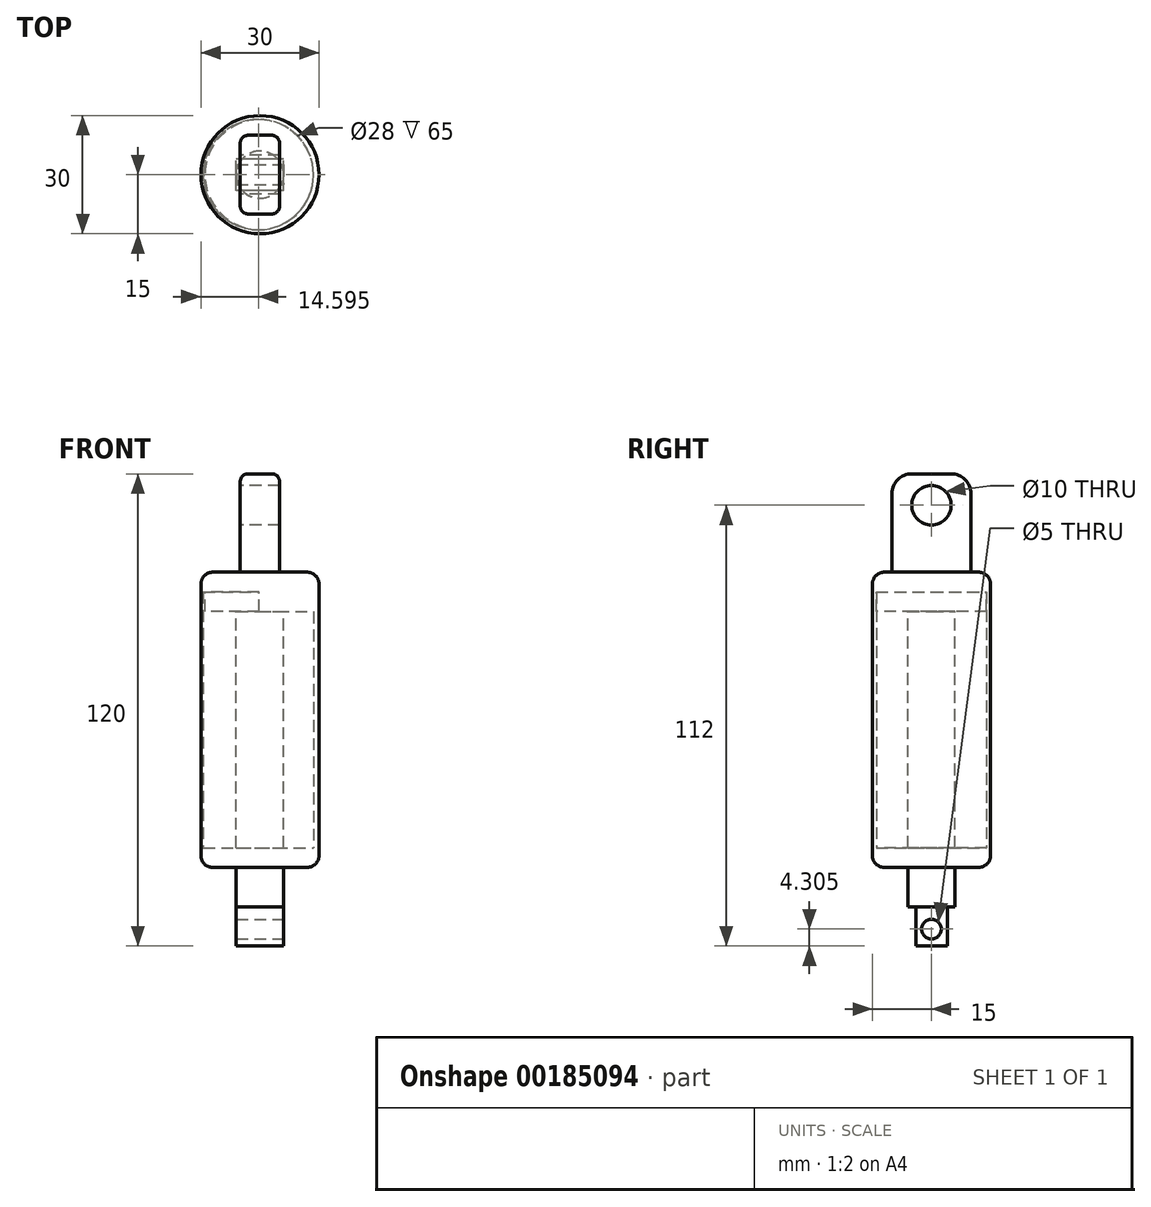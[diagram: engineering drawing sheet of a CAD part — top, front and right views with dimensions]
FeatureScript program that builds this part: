
annotation { "Feature Type Name" : "Feature", "Feature Type Description" : "" }
export const myFeature = defineFeature(function(context is Context, id is Id, definition is map)
    precondition{}
    {
        {
            var Q0;
            Q0=qCreatedBy(makeId("Top.planeOp"),FACE);
            var sketch = newSketch(context, id + "F0", { "sketchPlane" : qUnion([Q0])});
            skCircle(sketch, "E0", {"center": v(0, 0) * mm, "radius": 15 * mm});
            skSolve(sketch);
        }
        {
            var Q0;
            Q0 = qSketchRegion(id + "F0", true);
            extrude(context, id + "F1", {"entities" : qUnion([Q0]), "depth" : 70 * mm});
        }
        {
            var Q0;
            Q0=makeQuery(id+"F1.opExtrude","CAP_FACE",FACE,{"disambiguationData":[OSD([sQuery(id+"F0.wireOp",EDGE,"E0")])],"isStart":true});
            var sketch = newSketch(context, id + "F2", { "sketchPlane" : qUnion([Q0])});
            skCircle(sketch, "E1", {"center": v(-0.4, 0) * mm, "radius": 14 * mm});
            skSolve(sketch);
        }
        {
            var Q0;
            Q0 = qSketchRegion(id + "F2", true);
            extrude(context, id + "F3", {"entities" : qUnion([Q0]), "operationType" : NewBodyOperationType.REMOVE, "oppositeDirection" : true, "depth" : 65 * mm});
        }
        {
            var Q0;
            Q0=makeQuery(id+"F1.opExtrude","CAP_FACE",FACE,{"disambiguationData":[OSD([sQuery(id+"F0.wireOp",EDGE,"E0")])],"isStart":true});
            var sketch = newSketch(context, id + "F4", { "sketchPlane" : qUnion([Q0])});
            skCircle(sketch, "E2", {"center": v(0, 0) * mm, "radius": 15 * mm});
            skCircle(sketch, "E3", {"center": v(0, 0) * mm, "radius": 6 * mm});
            skSolve(sketch);
        }
        {
            var Q0;
            Q0=makeQuery(id+"F4.imprint","IMPRINT",FACE,{"disambiguationData":[TD([[makeQuery(id+"F4.imprint","IMPRINT",EDGE,{"derivedFrom":sQuery(id+"F4.wireOp",EDGE,"E2")}),-1.0]])]});
            var Q1;
            Q1=makeQuery(id+"F4.imprint","IMPRINT",FACE,{"disambiguationData":[TD([[makeQuery(id+"F4.imprint","IMPRINT",EDGE,{"derivedFrom":sQuery(id+"F4.wireOp",EDGE,"E3")}),-1.0]])]});
            extrude(context, id + "F5", {"entities" : qUnion([Q0, Q1]), "operationType" : NewBodyOperationType.ADD, "depth" : 5 * mm});
        }
        {
            var Q0;
            Q0=makeQuery(id+"F1.opExtrude","CAP_FACE",FACE,{"disambiguationData":[OSD([sQuery(id+"F0.wireOp",EDGE,"E0")])],"isStart":false});
            var sketch = newSketch(context, id + "F6", { "sketchPlane" : qUnion([Q0])});
            skLineSegment(sketch, "E4.bottom", {"start": v(5, 10) * mm, "end": v(-5, 10) * mm});
            skLineSegment(sketch, "E4.top", {"start": v(5, -10) * mm, "end": v(-5, -10) * mm});
            skLineSegment(sketch, "E4.left", {"start": v(5, 10) * mm, "end": v(5, -10) * mm});
            skLineSegment(sketch, "E4.right", {"start": v(-5, 10) * mm, "end": v(-5, -10) * mm});
            skPoint(sketch, "E4.middle", {"position": v(0, 0) * mm});
            skSolve(sketch);
        }
        {
            var Q0;
            Q0 = qSketchRegion(id + "F6", true);
            extrude(context, id + "F7", {"entities" : qUnion([Q0]), "operationType" : NewBodyOperationType.ADD, "depth" : 25 * mm});
        }
        {
            var Q0;
            Q0=makeQuery(id+"F7.opExtrude","SWEPT_FACE",FACE,{"disambiguationData":[OSD([sQuery(id+"F6.wireOp",EDGE,"E4.right")])]});
            var sketch = newSketch(context, id + "F8", { "sketchPlane" : qUnion([Q0])});
            skCircle(sketch, "E5", {"center": v(0, 87) * mm, "radius": 5 * mm});
            skSolve(sketch);
        }
        {
            var Q0;
            Q0 = qSketchRegion(id + "F8", true);
            extrude(context, id + "F9", {"entities" : qUnion([Q0]), "operationType" : NewBodyOperationType.REMOVE, "oppositeDirection" : true, "depth" : 25 * mm});
        }
        {
            var Q0;
            Q0=makeQuery(id+"F7.opExtrude","CAP_EDGE",EDGE,{"disambiguationData":[OSD([sQuery(id+"F6.wireOp",EDGE,"E4.bottom")])],"isStart":false});
            var Q1;
            Q1=makeQuery(id+"F7.opExtrude","CAP_EDGE",EDGE,{"disambiguationData":[OSD([sQuery(id+"F6.wireOp",EDGE,"E4.top")])],"isStart":false});
            fillet(context, id + "F10", {"entities" : qUnion([Q0, Q1]), "radius" : 5 * mm, "tangentPropagation" : true, "allowEdgeOverflow" : false});
        }
        {
            var Q0;
            Q0=makeQuery(id+"F7.opExtrude","SWEPT_EDGE",EDGE,{"disambiguationData":[OSD([sQuery(id+"F6.wireOp",EDGE,"E4.bottom"),sQuery(id+"F6.wireOp",EDGE,"E4.right")])]});
            var Q1;
            Q1=makeQuery(id+"F7.opExtrude","SWEPT_EDGE",EDGE,{"disambiguationData":[OSD([sQuery(id+"F6.wireOp",EDGE,"E4.bottom"),sQuery(id+"F6.wireOp",EDGE,"E4.left")])]});
            var Q2;
            Q2=makeQuery(id+"F7.opExtrude","CAP_EDGE",EDGE,{"disambiguationData":[OSD([sQuery(id+"F6.wireOp",EDGE,"E4.left")])],"isStart":true});
            fillet(context, id + "F11", {"entities" : qUnion([Q0, Q1, Q2]), "radius" : 2 * mm, "tangentPropagation" : true, "allowEdgeOverflow" : false});
        }
        {
            var Q0;
            Q0=makeQuery(id+"F3.boolean.opBoolean","COPY",FACE,{"derivedFrom":makeQuery(id+"F3.opExtrude","CAP_FACE",FACE,{"disambiguationData":[OSD([sQuery(id+"F2.wireOp",EDGE,"E1")])],"isStart":false})});
            var sketch = newSketch(context, id + "F12", { "sketchPlane" : qUnion([Q0])});
            skCircle(sketch, "E6", {"center": v(0, 0) * mm, "radius": 14 * mm});
            skSolve(sketch);
        }
        {
            var Q0;
            Q0 = qSketchRegion(id + "F12", true);
            extrude(context, id + "F13", {"entities" : qUnion([Q0]), "depth" : 5 * mm});
        }
        {
            var Q0;
            Q0=makeQuery(id+"F13.opExtrude","CAP_FACE",FACE,{"disambiguationData":[OSD([sQuery(id+"F12.wireOp",EDGE,"E6")])],"isStart":false});
            var sketch = newSketch(context, id + "F14", { "sketchPlane" : qUnion([Q0])});
            skCircle(sketch, "E7", {"center": v(0, 0) * mm, "radius": 6 * mm});
            skSolve(sketch);
        }
        {
            var Q0;
            Q0 = qSketchRegion(id + "F14", true);
            extrude(context, id + "F15", {"entities" : qUnion([Q0]), "operationType" : NewBodyOperationType.ADD, "depth" : 75 * mm});
        }
        {
            var Q0;
            Q0=makeQuery(id+"F15.opExtrude","CAP_FACE",FACE,{"disambiguationData":[OSD([sQuery(id+"F14.wireOp",EDGE,"E7")])],"isStart":false});
            var sketch = newSketch(context, id + "F16", { "sketchPlane" : qUnion([Q0])});
            skLineSegment(sketch, "E8.bottom", {"start": v(6, 4) * mm, "end": v(-6, 4) * mm});
            skLineSegment(sketch, "E8.top", {"start": v(6, -4) * mm, "end": v(-6, -4) * mm});
            skLineSegment(sketch, "E8.left", {"start": v(6, 4) * mm, "end": v(6, -4) * mm});
            skLineSegment(sketch, "E8.right", {"start": v(-6, 4) * mm, "end": v(-6, -4) * mm});
            skPoint(sketch, "E8.middle", {"position": v(0, 0) * mm});
            skSolve(sketch);
        }
        {
            var Q0;
            {var subQ0=sQuery(id+"F16.wireOp",EDGE,"E8.left");var subQ1=sQuery(id+"F16.wireOp",EDGE,"E8.bottom");var subQ2=makeQuery(id+"F16.imprint","INTERSECT",VERTEX,{"derivedFrom":[subQ1,subQ0]});Q0=makeQuery(id+"F16.imprint","IMPRINT",FACE,{"disambiguationData":[TD([[makeQuery(id+"F16.imprint","IMPRINT",EDGE,{"disambiguationData":[TD([[subQ2,-1.0]])],"derivedFrom":subQ1}),1.0]])]});}
            var Q1;
            {var subQ0=sQuery(id+"F16.wireOp",EDGE,"E8.bottom");var subQ1=makeQuery(id+"F15.opExtrude","CAP_EDGE",EDGE,{"disambiguationData":[OSD([sQuery(id+"F14.wireOp",EDGE,"E7")])],"isStart":false});var subQ4=makeQuery(id+"F16.imprint","INTERSECT",VERTEX,{"disambiguationData":[OD(0.0)],"derivedFrom":[subQ1,subQ0]});Q1=makeQuery(id+"F16.imprint","IMPRINT",FACE,{"disambiguationData":[TD([[makeQuery(id+"F16.imprint","IMPRINT",EDGE,{"disambiguationData":[TD([[subQ4,-1.0]])],"derivedFrom":subQ0}),1.0]])]});}
            var Q2;
            {var subQ0=sQuery(id+"F16.wireOp",EDGE,"E8.right");var subQ1=sQuery(id+"F16.wireOp",EDGE,"E8.bottom");var subQ2=makeQuery(id+"F16.imprint","INTERSECT",VERTEX,{"derivedFrom":[subQ1,subQ0]});Q2=makeQuery(id+"F16.imprint","IMPRINT",FACE,{"disambiguationData":[TD([[makeQuery(id+"F16.imprint","IMPRINT",EDGE,{"disambiguationData":[TD([[subQ2,1.0]])],"derivedFrom":subQ1}),1.0]])]});}
            var Q3;
            {var subQ0=sQuery(id+"F16.wireOp",EDGE,"E8.right");var subQ1=sQuery(id+"F16.wireOp",EDGE,"E8.top");var subQ2=makeQuery(id+"F16.imprint","INTERSECT",VERTEX,{"derivedFrom":[subQ1,subQ0]});Q3=makeQuery(id+"F16.imprint","IMPRINT",FACE,{"disambiguationData":[TD([[makeQuery(id+"F16.imprint","IMPRINT",EDGE,{"disambiguationData":[TD([[subQ2,1.0]])],"derivedFrom":subQ1}),-1.0]])]});}
            var Q4;
            {var subQ0=sQuery(id+"F16.wireOp",EDGE,"E8.left");var subQ1=sQuery(id+"F16.wireOp",EDGE,"E8.top");var subQ2=makeQuery(id+"F16.imprint","INTERSECT",VERTEX,{"derivedFrom":[subQ1,subQ0]});Q4=makeQuery(id+"F16.imprint","IMPRINT",FACE,{"disambiguationData":[TD([[makeQuery(id+"F16.imprint","IMPRINT",EDGE,{"disambiguationData":[TD([[subQ2,-1.0]])],"derivedFrom":subQ1}),-1.0]])]});}
            extrude(context, id + "F17", {"entities" : qUnion([Q0, Q1, Q2, Q3, Q4]), "operationType" : NewBodyOperationType.ADD, "depth" : 10 * mm});
        }
        {
            var Q0;
            Q0=makeQuery(id+"F17.opExtrude","SWEPT_FACE",FACE,{"disambiguationData":[OSD([sQuery(id+"F16.wireOp",EDGE,"E8.left")])]});
            var sketch = newSketch(context, id + "F18", { "sketchPlane" : qUnion([Q0])});
            skCircle(sketch, "E9", {"center": v(0, -20.7) * mm, "radius": 2.5 * mm});
            skSolve(sketch);
        }
        {
            var Q0;
            Q0 = qSketchRegion(id + "F18", true);
            extrude(context, id + "F19", {"entities" : qUnion([Q0]), "operationType" : NewBodyOperationType.REMOVE, "oppositeDirection" : true, "depth" : 25 * mm});
        }
        {
            var Q0;
            Q0=makeQuery(id+"F5.opExtrude","CAP_EDGE",EDGE,{"disambiguationData":[OSD([sQuery(id+"F4.wireOp",EDGE,"E2")])],"isStart":false});
            var Q1;
            Q1=makeQuery(id+"F1.opExtrude","CAP_EDGE",EDGE,{"disambiguationData":[OSD([sQuery(id+"F0.wireOp",EDGE,"E0")])],"isStart":false});
            fillet(context, id + "F20", {"entities" : qUnion([Q0, Q1]), "radius" : 3 * mm, "tangentPropagation" : true, "allowEdgeOverflow" : false});
        }
    });
